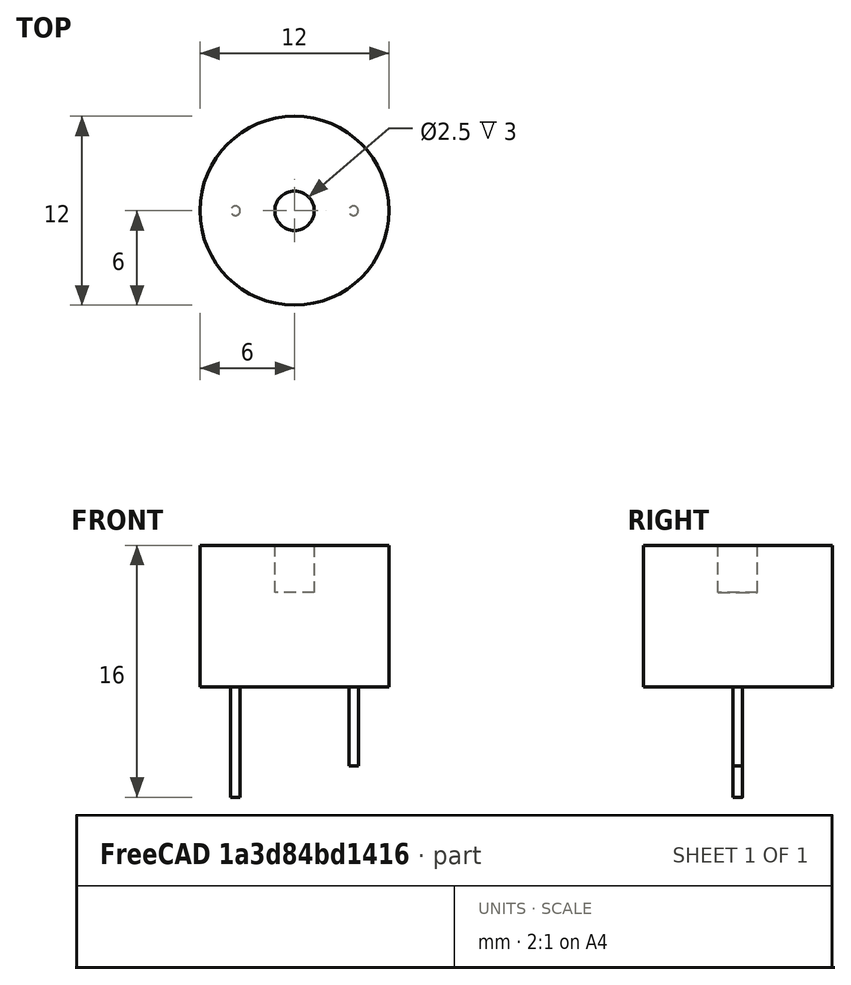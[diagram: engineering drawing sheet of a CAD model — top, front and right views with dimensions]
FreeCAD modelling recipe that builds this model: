
FCSTD DOCUMENT  (FreeCAD 0.14R3692 (Git))
Label: buzzer
License: The MIT License
LicenseURL: http://opensource.org/licenses/MIT
objects: Part::Cylinder×3, Sketcher::SketchObject×1, PartDesign::Pocket×1, Part::MultiFuse×1
note: 7 computed .brp shape members not serialized (recipe doc carries the construction recipe); baked Part::Feature solids carry a one-line shape summary decoded from their .brp

FEATURE [Part::Cylinder] Cylinder  label="body-cylinder"
  Angle = 360
  Height = 9
  Radius = 6
FEATURE [Sketcher::SketchObject] Sketch  label="hole-sketch"
  Placement = pos=(0,0,9) rot=(0,0,1;0rad)
  Support = -> Cylinder [Face2]
  sketch-geometry (1):
    g0: Circle CenterX=0 CenterY=0 CenterZ=0 NormalX=0 NormalY=0 NormalZ=1 Radius=1.25
  constraints (2):
    c: Coincident(g0,g-1)
    c: Radius(g0) = 1.25
FEATURE [PartDesign::Pocket] Pocket  label="hole-pocket"
  Length = 3
  Sketch = -> Sketch
  Type = 0
FEATURE [Part::Cylinder] Cylinder001  label="anode-cylinder"
  Angle = 360
  Height = 7
  Placement = pos=(-3.75,0,-7) rot=(0,0,1;0rad)
  Radius = 0.3
FEATURE [Part::Cylinder] Cylinder002  label="cathode-cylinder"
  Angle = 360
  Height = 5
  Placement = pos=(3.75,0,-5) rot=(0,0,1;0rad)
  Radius = 0.3
FEATURE [Part::MultiFuse] Fusion  label="buzzer"
  Shapes = -> [Cylinder001,Pocket,Cylinder002]
